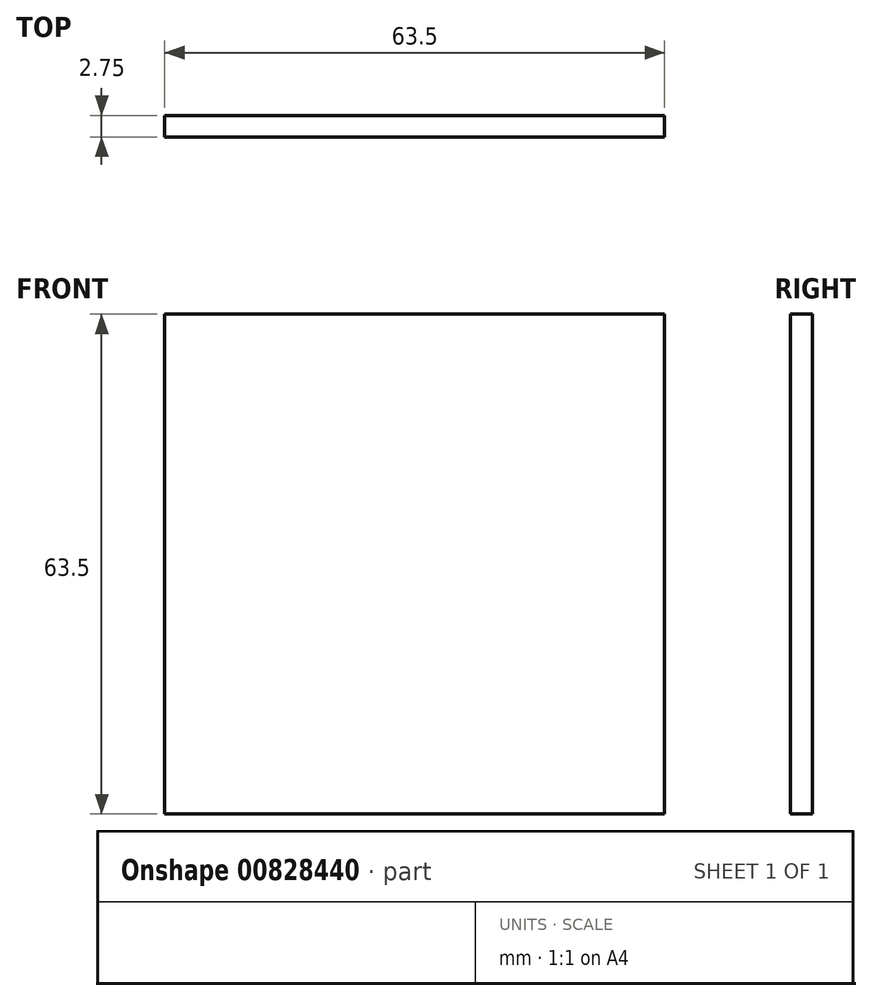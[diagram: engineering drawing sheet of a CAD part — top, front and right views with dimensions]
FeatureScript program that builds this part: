
annotation { "Feature Type Name" : "Feature", "Feature Type Description" : "" }
export const myFeature = defineFeature(function(context is Context, id is Id, definition is map)
    precondition{}
    {
        {
            var Q0;
            Q0=qCreatedBy(makeId("Front.planeOp"),FACE);
            var sketch = newSketch(context, id + "F0", { "sketchPlane" : qUnion([Q0])});
            skLineSegment(sketch, "E0.bottom", {"start": v(0, 0) * mm, "end": v(63.5, 0) * mm});
            skLineSegment(sketch, "E0.top", {"start": v(0, 63.5) * mm, "end": v(63.5, 63.5) * mm});
            skLineSegment(sketch, "E0.left", {"start": v(0, 0) * mm, "end": v(0, 63.5) * mm});
            skLineSegment(sketch, "E0.right", {"start": v(63.5, 0) * mm, "end": v(63.5, 63.5) * mm});
            skSolve(sketch);
        }
        {
            var Q0;
            Q0 = qSketchRegion(id + "F0", true);
            extrude(context, id + "F1", {"entities" : qUnion([Q0]), "depth" : 2.75 * mm, "offsetDistance" : 25.4 * mm});
        }
    });
